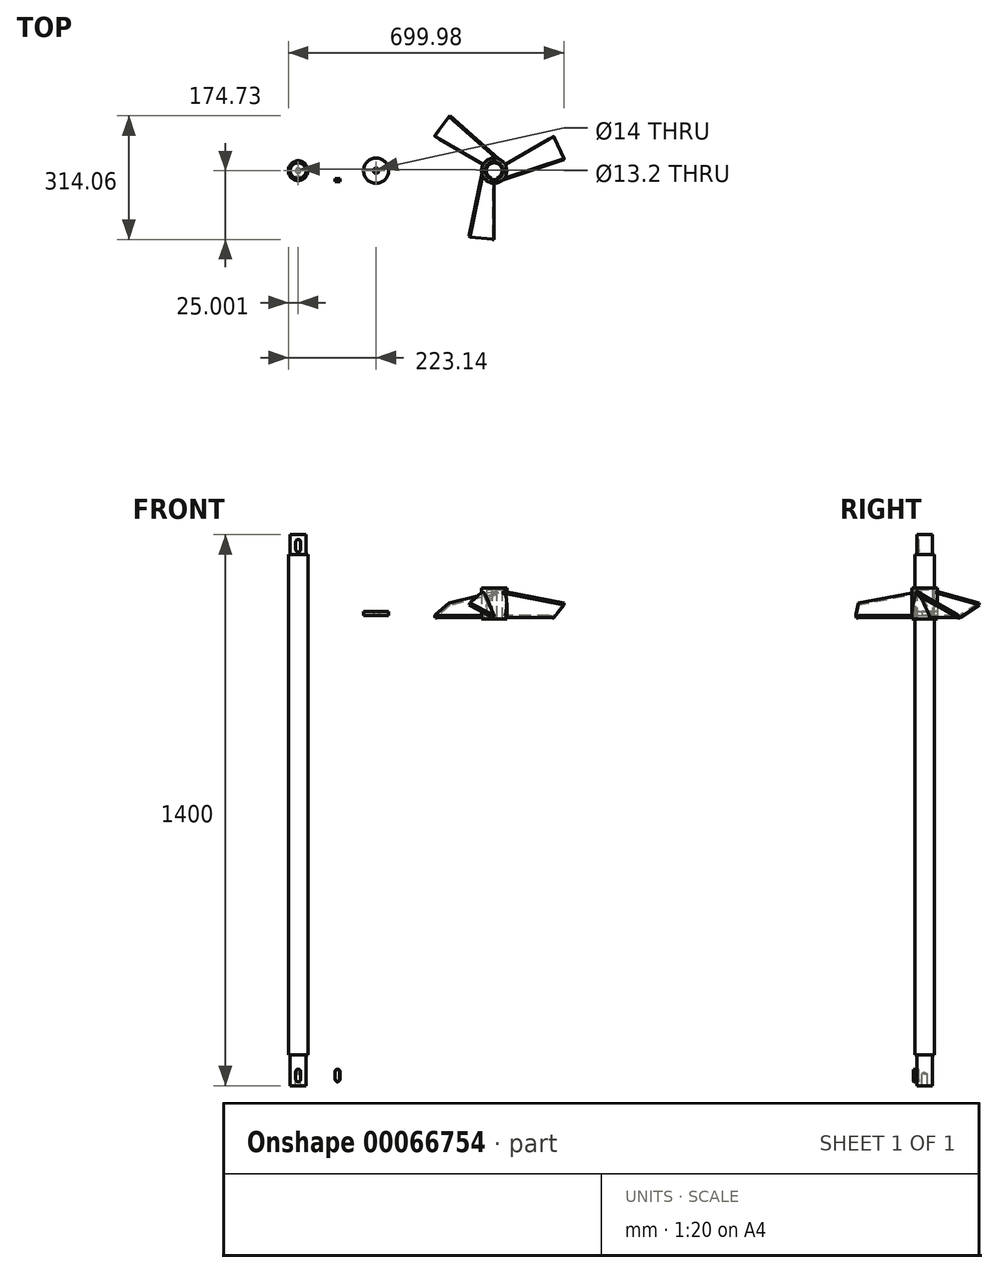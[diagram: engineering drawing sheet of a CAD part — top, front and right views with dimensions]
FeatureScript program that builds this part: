
annotation { "Feature Type Name" : "Feature", "Feature Type Description" : "" }
export const myFeature = defineFeature(function(context is Context, id is Id, definition is map)
    precondition{}
    {
        {
            assignVariable(context, id + "F0", {"name" : "D2", "anyValue" : 70});
        }
        {
            assignVariable(context, id + "F1", {"name" : "D3", "anyValue" : 67});
        }
        {
            assignVariable(context, id + "F2", {"name" : "D4", "anyValue" : 25});
        }
        {
            assignVariable(context, id + "F3", {"name" : "D7", "anyValue" : 40});
        }
        {
            assignVariable(context, id + "F4", {"name" : "D10", "anyValue" : 5});
        }
        {
            assignVariable(context, id + "F5", {"name" : "D12", "anyValue" : 8});
        }
        {
            assignVariable(context, id + "F6", {"name" : "D13", "anyValue" : .4});
        }
        {
            var Q0;
            Q0=qCreatedBy(makeId("Top.planeOp"),FACE);
            var sketch = newSketch(context, id + "F7", { "sketchPlane" : qUnion([Q0])});
            skLineSegment(sketch, "E0", {"start": v(0, 0) * mm, "end": v(0, -175) * mm, "construction": true});
            skSolve(sketch);
        }
        {
            var Q0;
            Q0=sQuery(id+"F7.wireOp",EDGE,"E0");
            cPlane(context, id + "F8", {"entities" : qUnion([Q0]), "cplaneType" : CPlaneType.LINE_ANGLE, "offset" : 150 * mm, "angle" : (180 - getVariable(context, 'D3')) * degree, "width" : 150 * mm, "height" : 150 * mm});
        }
        {
            var Q0;
            Q0=qCreatedBy(id+"F8.planeOp",FACE);
            var sketch = newSketch(context, id + "F9", { "sketchPlane" : qUnion([Q0])});
            skLineSegment(sketch, "E1", {"start": v(0, 0) * mm, "end": v(0, 70) * mm});
            skLineSegment(sketch, "E2", {"start": v(0, 70) * mm, "end": v(-175, 0) * mm});
            skLineSegment(sketch, "E3", {"start": v(-175, 0) * mm, "end": v(0, 0) * mm});
            skSolve(sketch);
        }
        {
            var Q0;
            Q0=sQuery(id+"F9.wireOp",EDGE,"E2");
            cPlane(context, id + "F10", {"entities" : qUnion([Q0]), "cplaneType" : CPlaneType.LINE_ANGLE, "offset" : 150 * mm, "angle" : (180 - getVariable(context, 'D4')) * degree, "width" : 150 * mm, "height" : 150 * mm});
        }
        {
            var Q0;
            Q0=qCreatedBy(id+"F10.planeOp",FACE);
            var sketch = newSketch(context, id + "F11", { "sketchPlane" : qUnion([Q0])});
            skLineSegment(sketch, "E4", {"start": v(-50.7, 18.13) * mm, "end": v(-20.6, -167.93) * mm});
            skLineSegment(sketch, "E5", {"start": v(-88.9, -152.65) * mm, "end": v(-20.6, -167.93) * mm});
            skLineSegment(sketch, "E6", {"start": v(-50.7, 18.13) * mm, "end": v(-88.9, -152.65) * mm});
            skSolve(sketch);
        }
        {
            var Q0;
            Q0=makeQuery(id+"F11.imprint","IMPRINT",FACE,{"disambiguationData":[TD([[makeQuery(id+"F11.imprint","IMPRINT",EDGE,{"derivedFrom":sQuery(id+"F11.wireOp",EDGE,"E4")}),-1.0]])]});
            var Q1;
            Q1=makeQuery(id+"F9.imprint","IMPRINT",FACE,{"disambiguationData":[TD([[makeQuery(id+"F9.imprint","IMPRINT",EDGE,{"derivedFrom":sQuery(id+"F9.wireOp",EDGE,"E1")}),1.0]])]});
            extrude(context, id + "F12", {"entities" : qUnion([Q0, Q1]), "oppositeDirection" : true, "depth" : 6 * mm});
        }
        {
            var Q0;
            Q0=qCreatedBy(makeId("Top.planeOp"),FACE);
            var sketch = newSketch(context, id + "F13", { "sketchPlane" : qUnion([Q0])});
            skCircle(sketch, "E7", {"center": v(0, 0) * mm, "radius": 32 * mm});
            skSolve(sketch);
        }
        {
            var Q0;
            Q0=makeQuery(id+"F13.imprint","IMPRINT",FACE,{"disambiguationData":[TD([[makeQuery(id+"F13.imprint","IMPRINT",EDGE,{"derivedFrom":sQuery(id+"F13.wireOp",EDGE,"E7")}),1.0]])]});
            extrude(context, id + "F14", {"entities" : qUnion([Q0]), "operationType" : NewBodyOperationType.REMOVE, "depth" : 200 * mm, "symmetric" : true});
        }
        {
            var Q0;
            Q0=qCreatedBy(makeId("Top.planeOp"),FACE);
            var sketch = newSketch(context, id + "F15", { "sketchPlane" : qUnion([Q0])});
            skCircle(sketch, "E8", {"center": v(0, 0) * mm, "radius": 20 * mm});
            skCircle(sketch, "E9", {"center": v(0, 0) * mm, "radius": 32 * mm});
            skSolve(sketch);
        }
        {
            var Q0;
            Q0=makeQuery(id+"F15.imprint","IMPRINT",FACE,{"disambiguationData":[TD([[makeQuery(id+"F15.imprint","IMPRINT",EDGE,{"derivedFrom":sQuery(id+"F15.wireOp",EDGE,"E8")}),-1.0]])]});
            extrude(context, id + "F16", {"entities" : qUnion([Q0]), "depth" : (getVariable(context, 'D2')) * mm, "hasSecondDirection" : true, "secondDirectionOppositeDirection" : true, "secondDirectionDepth" : 8 * mm});
        }
        {
            var Q0;
            Q0=makeQuery(id+"F16.opExtrude","CAP_EDGE",EDGE,{"disambiguationData":[OSD([sQuery(id+"F15.wireOp",EDGE,"E8")])],"isStart":false});
            chamfer(context, id + "F17", {"entities" : qUnion([Q0]), "width" : 3 * mm, "tangentPropagation" : true});
        }
        {
            var Q0;
            Q0=makeQuery(id+"F12.opExtrude","SWEPT_BODY",BODY,{"disambiguationData":[OSD([sQuery(id+"F9.wireOp",EDGE,"E1"),sQuery(id+"F9.wireOp",EDGE,"E2"),sQuery(id+"F9.wireOp",EDGE,"E3")])]});
            var Q1;
            Q1=makeQuery(id+"F12.opExtrude","SWEPT_BODY",BODY,{"disambiguationData":[OSD([sQuery(id+"F11.wireOp",EDGE,"E4"),sQuery(id+"F11.wireOp",EDGE,"E5"),sQuery(id+"F11.wireOp",EDGE,"E6")])]});
            booleanBodies(context, id + "F18", {"operationType" : BooleanOperationType.UNION, "tools" : qUnion([Q0, Q1])});
        }
        {
            var Q0;
            Q0=makeQuery(id+"F18.opBoolean","MERGE",EDGE,{"derivedFrom":[makeQuery(id+"F12.opExtrude","CAP_EDGE",EDGE,{"disambiguationData":[OSD([sQuery(id+"F11.wireOp",EDGE,"E4")])],"isStart":false}),makeQuery(id+"F12.opExtrude","CAP_EDGE",EDGE,{"disambiguationData":[OSD([sQuery(id+"F9.wireOp",EDGE,"E2")]),OD(0.0)],"isStart":false})]});
            fillet(context, id + "F19", {"entities" : qUnion([Q0]), "radius" : 5 * mm, "tangentPropagation" : true, "allowEdgeOverflow" : false});
        }
        {
            var Q0;
            Q0=makeQuery(id+"F18.opBoolean","MERGE",EDGE,{"derivedFrom":[makeQuery(id+"F12.opExtrude","CAP_EDGE",EDGE,{"disambiguationData":[OSD([sQuery(id+"F11.wireOp",EDGE,"E4")])],"isStart":true}),makeQuery(id+"F12.opExtrude","CAP_EDGE",EDGE,{"disambiguationData":[OSD([sQuery(id+"F9.wireOp",EDGE,"E2")]),OD(1.0)],"isStart":false})]});
            fillet(context, id + "F20", {"entities" : qUnion([Q0]), "radius" : 13 * mm, "tangentPropagation" : true, "allowEdgeOverflow" : false});
        }
        {
            var Q0;
            Q0=makeQuery(id+"F12.opExtrude","SWEPT_BODY",BODY,{"disambiguationData":[OSD([sQuery(id+"F9.wireOp",EDGE,"E1"),sQuery(id+"F9.wireOp",EDGE,"E2"),sQuery(id+"F9.wireOp",EDGE,"E3")])]});
            var Q1;
            Q1=makeQuery(id+"F16.opExtrude","CAP_EDGE",EDGE,{"disambiguationData":[OSD([sQuery(id+"F15.wireOp",EDGE,"E9")])],"isStart":true});
            circularPattern(context, id + "F21", {"entities" : qUnion([Q0]), "axis" : qUnion([Q1]), "angle" : 360 * degree, "instanceCount" : round(3), "equalSpace" : true});
        }
        {
            var Q0;
            Q0=qCreatedBy(makeId("Front.planeOp"),FACE);
            var sketch = newSketch(context, id + "F22", { "sketchPlane" : qUnion([Q0])});
            skLineSegment(sketch, "E10", {"start": v(-498.14, 205.86) * mm, "end": v(-498.14, -1194.14) * mm});
            skLineSegment(sketch, "E11", {"start": v(-523.14, -1116.14) * mm, "end": v(-523.14, 155.86) * mm});
            skLineSegment(sketch, "E12", {"start": v(-518.14, 205.86) * mm, "end": v(-498.14, 205.86) * mm});
            skLineSegment(sketch, "E13", {"start": v(-523.14, -1116.14) * mm, "end": v(-518.64, -1116.14) * mm});
            skLineSegment(sketch, "E14", {"start": v(-518.14, -1116.64) * mm, "end": v(-518.14, -1194.14) * mm});
            skLineSegment(sketch, "E15", {"start": v(-518.14, -1194.14) * mm, "end": v(-498.14, -1194.14) * mm});
            skPoint(sketch, "E16.visualSharp", {"position": v(-518.14, -1116.14) * mm});
            skArc(sketch, "E16.filletArc", {"start": v(-518.14, -1116.64) * mm, "mid": v(-518.29, -1116.28) * mm, "end": v(-518.64, -1116.14) * mm});
            skLineSegment(sketch, "E17", {"start": v(-523.14, 155.86) * mm, "end": v(-518.64, 155.86) * mm});
            skLineSegment(sketch, "E18", {"start": v(-518.14, 156.36) * mm, "end": v(-518.14, 205.86) * mm});
            skPoint(sketch, "E19.visualSharp", {"position": v(-518.14, 155.86) * mm});
            skArc(sketch, "E19.filletArc", {"start": v(-518.64, 155.86) * mm, "mid": v(-518.29, 156.01) * mm, "end": v(-518.14, 156.36) * mm});
            skSolve(sketch);
        }
        {
            var Q0;
            Q0=makeQuery(id+"F22.imprint","IMPRINT",FACE,{"disambiguationData":[TD([[makeQuery(id+"F22.imprint","IMPRINT",EDGE,{"derivedFrom":sQuery(id+"F22.wireOp",EDGE,"E10")}),-1.0]])]});
            var Q1;
            Q1=sQuery(id+"F22.wireOp",EDGE,"E10");
            revolve(context, id + "F23", {"entities" : qUnion([Q0]), "axis" : qUnion([Q1]), "revolveType" : RevolveType.FULL});
        }
        {
            var Q0;
            Q0=makeQuery(id+"F22.imprint","IMPRINT",FACE,{"disambiguationData":[TD([[makeQuery(id+"F22.imprint","IMPRINT",EDGE,{"derivedFrom":sQuery(id+"F22.wireOp",EDGE,"E10")}),-1.0]])]});
            cPlane(context, id + "F24", {"entities" : qUnion([Q0]), "cplaneType" : CPlaneType.OFFSET, "offset" : (getVariable(context, 'D7') / 2) * mm, "width" : 150 * mm, "height" : 150 * mm});
        }
        {
            var Q0;
            Q0=qCreatedBy(id+"F24.planeOp",FACE);
            var sketch = newSketch(context, id + "F25", { "sketchPlane" : qUnion([Q0])});
            skLineSegment(sketch, "E20", {"start": v(-504.14, -1178.14) * mm, "end": v(-504.14, -1158.14) * mm});
            skLineSegment(sketch, "E21", {"start": v(-498.14, -1194.14) * mm, "end": v(-498.14, -1158.14) * mm, "construction": true});
            skLineSegment(sketch, "E22.MirrorCS", {"start": v(-492.14, -1178.14) * mm, "end": v(-492.14, -1158.14) * mm});
            skArc(sketch, "E23", {"start": v(-504.14, -1158.14) * mm, "mid": v(-498.14, -1152.14) * mm, "end": v(-492.14, -1158.14) * mm});
            skArc(sketch, "E24", {"start": v(-492.14, -1178.14) * mm, "mid": v(-498.14, -1184.14) * mm, "end": v(-504.14, -1178.14) * mm});
            skLineSegment(sketch, "E25", {"start": v(-504.14, 167.86) * mm, "end": v(-504.14, 187.86) * mm});
            skLineSegment(sketch, "E26.MirrorCS", {"start": v(-492.14, 167.86) * mm, "end": v(-492.14, 187.86) * mm});
            skArc(sketch, "E27", {"start": v(-504.14, 187.86) * mm, "mid": v(-498.14, 193.86) * mm, "end": v(-492.14, 187.86) * mm});
            skArc(sketch, "E28", {"start": v(-492.14, 167.86) * mm, "mid": v(-498.14, 161.86) * mm, "end": v(-504.14, 167.86) * mm});
            skSolve(sketch);
        }
        {
            var Q0;
            Q0=makeQuery(id+"F25.imprint","IMPRINT",FACE,{"disambiguationData":[TD([[makeQuery(id+"F25.imprint","IMPRINT",EDGE,{"derivedFrom":sQuery(id+"F25.wireOp",EDGE,"E20")}),-1.0]])]});
            extrude(context, id + "F26", {"entities" : qUnion([Q0]), "operationType" : NewBodyOperationType.REMOVE, "oppositeDirection" : true, "depth" : (getVariable(context, 'D10')) * mm});
        }
        {
            var Q0;
            Q0=makeQuery(id+"F23.opRevolve","SWEPT_FACE",FACE,{"disambiguationData":[OSD([sQuery(id+"F22.wireOp",EDGE,"E15")])]});
            var sketch = newSketch(context, id + "F27", { "sketchPlane" : qUnion([Q0])});
            skPoint(sketch, "E29", {"position": v(-498.14, 0) * mm});
            skSolve(sketch);
        }
        {
            var Q0;
            Q0=makeQuery(id+"F16.opExtrude","CAP_FACE",FACE,{"disambiguationData":[OSD([sQuery(id+"F15.wireOp",EDGE,"E8"),sQuery(id+"F15.wireOp",EDGE,"E9")])],"isStart":true});
            var sketch = newSketch(context, id + "F28", { "sketchPlane" : qUnion([Q0])});
            skLineSegment(sketch, "E30", {"start": v(-6, 19.08) * mm, "end": v(-6, 23.3) * mm});
            skLineSegment(sketch, "E31.MirrorCS", {"start": v(6, 19.08) * mm, "end": v(6, 23.3) * mm});
            skLineSegment(sketch, "E32", {"start": v(-6, 23.3) * mm, "end": v(6, 23.3) * mm});
            skArc(sketch, "E33", {"start": v(-6, 19.08) * mm, "mid": v(0, 20) * mm, "end": v(6, 19.08) * mm});
            skPoint(sketch, "E34.orphan", {"position": v(-6, 16.2) * mm});
            skPoint(sketch, "E35.orphan", {"position": v(6, 16.2) * mm});
            skSolve(sketch);
        }
        {
            var Q0;
            Q0=makeQuery(id+"F28.imprint","IMPRINT",FACE,{"disambiguationData":[TD([[makeQuery(id+"F28.imprint","IMPRINT",EDGE,{"derivedFrom":sQuery(id+"F28.wireOp",EDGE,"E30")}),-1.0]])]});
            extrude(context, id + "F29", {"entities" : qUnion([Q0]), "operationType" : NewBodyOperationType.REMOVE, "endBound" : BoundingType.THROUGH_ALL, "oppositeDirection" : true, "depth" : 25 * mm});
        }
        {
            var Q0;
            Q0=qCreatedBy(id+"F24.planeOp",FACE);
            var sketch = newSketch(context, id + "F30", { "sketchPlane" : qUnion([Q0])});
            skLineSegment(sketch, "E36", {"start": v(-398.14, -1100.2) * mm, "end": v(-398.14, -1235.4) * mm, "construction": true});
            skArc(sketch, "E37", {"start": v(-392.14, -1158.14) * mm, "mid": v(-398.14, -1152.14) * mm, "end": v(-404.14, -1158.14) * mm});
            skArc(sketch, "E38", {"start": v(-404.14, -1178.14) * mm, "mid": v(-398.14, -1184.14) * mm, "end": v(-392.14, -1178.14) * mm});
            skLineSegment(sketch, "E39", {"start": v(-392.14, -1158.14) * mm, "end": v(-392.14, -1178.14) * mm});
            skLineSegment(sketch, "E40", {"start": v(-404.14, -1158.14) * mm, "end": v(-404.14, -1178.14) * mm});
            skSolve(sketch);
        }
        {
            var Q0;
            Q0=makeQuery(id+"F30.imprint","IMPRINT",FACE,{"disambiguationData":[TD([[makeQuery(id+"F30.imprint","IMPRINT",EDGE,{"derivedFrom":sQuery(id+"F30.wireOp",EDGE,"E37")}),1.0]])]});
            extrude(context, id + "F31", {"entities" : qUnion([Q0]), "depth" : (getVariable(context, 'D12')) * mm});
        }
        {
            var Q0;
            Q0=makeQuery(id+"F31.opExtrude","CAP_FACE",FACE,{"disambiguationData":[OSD([sQuery(id+"F30.wireOp",EDGE,"E37"),sQuery(id+"F30.wireOp",EDGE,"E38"),sQuery(id+"F30.wireOp",EDGE,"E39"),sQuery(id+"F30.wireOp",EDGE,"E40")])],"isStart":false});
            var Q1;
            Q1=makeQuery(id+"F31.opExtrude","CAP_FACE",FACE,{"disambiguationData":[OSD([sQuery(id+"F30.wireOp",EDGE,"E37"),sQuery(id+"F30.wireOp",EDGE,"E38"),sQuery(id+"F30.wireOp",EDGE,"E39"),sQuery(id+"F30.wireOp",EDGE,"E40")])],"isStart":true});
            chamfer(context, id + "F32", {"entities" : qUnion([Q0, Q1]), "width" : (getVariable(context, 'D13')) * mm, "tangentPropagation" : true});
        }
        {
            var Q0;
            Q0=qCreatedBy(makeId("Top.planeOp"),FACE);
            var sketch = newSketch(context, id + "F33", { "sketchPlane" : qUnion([Q0])});
            skCircle(sketch, "E41", {"center": v(-300, 0) * mm, "radius": 32 * mm});
            skCircle(sketch, "E42", {"center": v(-300, 0) * mm, "radius": 7 * mm});
            skSolve(sketch);
        }
        {
            var Q0;
            Q0=makeQuery(id+"F33.imprint","IMPRINT",FACE,{"disambiguationData":[TD([[makeQuery(id+"F33.imprint","IMPRINT",EDGE,{"derivedFrom":sQuery(id+"F33.wireOp",EDGE,"E41")}),1.0]])]});
            extrude(context, id + "F34", {"entities" : qUnion([Q0]), "depth" : 10 * mm});
        }
        {
            var Q0;
            Q0=sQuery(id+"F27.wireOp",VERTEX,"E29");
            var Q1;
            Q1=makeQuery(id+"F23.opRevolve","SWEPT_BODY",BODY,{"disambiguationData":[OSD([sQuery(id+"F22.wireOp",EDGE,"E10"),sQuery(id+"F22.wireOp",EDGE,"E11"),sQuery(id+"F22.wireOp",EDGE,"E12"),sQuery(id+"F22.wireOp",EDGE,"E13"),sQuery(id+"F22.wireOp",EDGE,"E14"),sQuery(id+"F22.wireOp",EDGE,"E15"),sQuery(id+"F22.wireOp",EDGE,"E16.filletArc"),sQuery(id+"F22.wireOp",EDGE,"E17"),sQuery(id+"F22.wireOp",EDGE,"E18")])]});
            hole(context, id + "F35", {"style" : HoleStyle.SIMPLE, "endStyle" : HoleEndStyle.BLIND, "standardTappedOrClearance" : lookupTablePath({ "standard" : "ISO", "fit" : "Normal", "size" : "M12", "type" : "Clearance" }), "standardBlindInLast" : lookupTablePath({ "fit" : "Standard", "standard" : "ISO", "size" : "M12", "type" : "Clearance" }), "holeDiameter" : 13.2 * mm, "holeDepth" : 30 * mm, "locations" : qUnion([Q0]), "scope" : qUnion([Q1]), "startStyle" : HoleStartStyle.SKETCH});
        }
        {
            var Q0;
            Q0=makeQuery(id+"F25.imprint","IMPRINT",FACE,{"disambiguationData":[TD([[makeQuery(id+"F25.imprint","IMPRINT",EDGE,{"derivedFrom":sQuery(id+"F25.wireOp",EDGE,"E25")}),-1.0]])]});
            extrude(context, id + "F36", {"entities" : qUnion([Q0]), "operationType" : NewBodyOperationType.REMOVE, "oppositeDirection" : true, "depth" : (getVariable(context, 'D10')) * mm});
        }
    });
